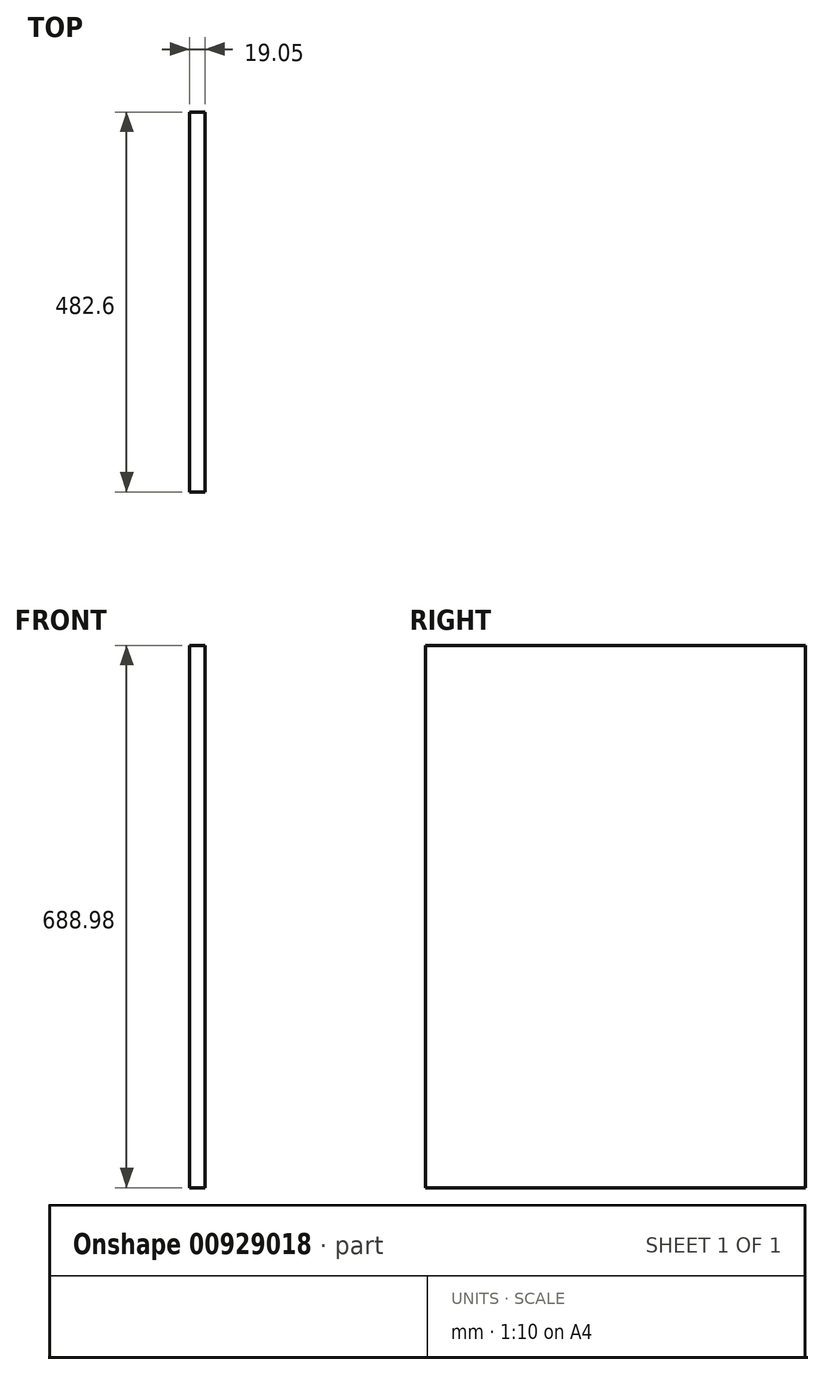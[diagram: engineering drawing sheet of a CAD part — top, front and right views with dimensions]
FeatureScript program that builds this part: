
annotation { "Feature Type Name" : "Feature", "Feature Type Description" : "" }
export const myFeature = defineFeature(function(context is Context, id is Id, definition is map)
    precondition{}
    {
        {
            var Q0;
            Q0=qCreatedBy(makeId("Right.planeOp"),FACE);
            var sketch = newSketch(context, id + "F0", { "sketchPlane" : qUnion([Q0])});
            skLineSegment(sketch, "E0.bottom", {"start": v(241.3, 344.49) * mm, "end": v(-241.3, 344.49) * mm});
            skLineSegment(sketch, "E0.top", {"start": v(241.3, -344.49) * mm, "end": v(-241.3, -344.49) * mm});
            skLineSegment(sketch, "E0.left", {"start": v(241.3, 344.49) * mm, "end": v(241.3, -344.49) * mm});
            skLineSegment(sketch, "E0.right", {"start": v(-241.3, 344.49) * mm, "end": v(-241.3, -344.49) * mm});
            skPoint(sketch, "E0.middle", {"position": v(0, 0) * mm});
            skSolve(sketch);
        }
        {
            var Q0;
            Q0=makeQuery(id+"F0.imprint","IMPRINT",FACE,{"disambiguationData":[TD([[makeQuery(id+"F0.imprint","IMPRINT",EDGE,{"derivedFrom":sQuery(id+"F0.wireOp",EDGE,"E0.bottom")}),1.0]])]});
            extrude(context, id + "F1", {"entities" : qUnion([Q0]), "depth" : 19.05 * mm, "offsetDistance" : 25.4 * mm});
        }
    });
